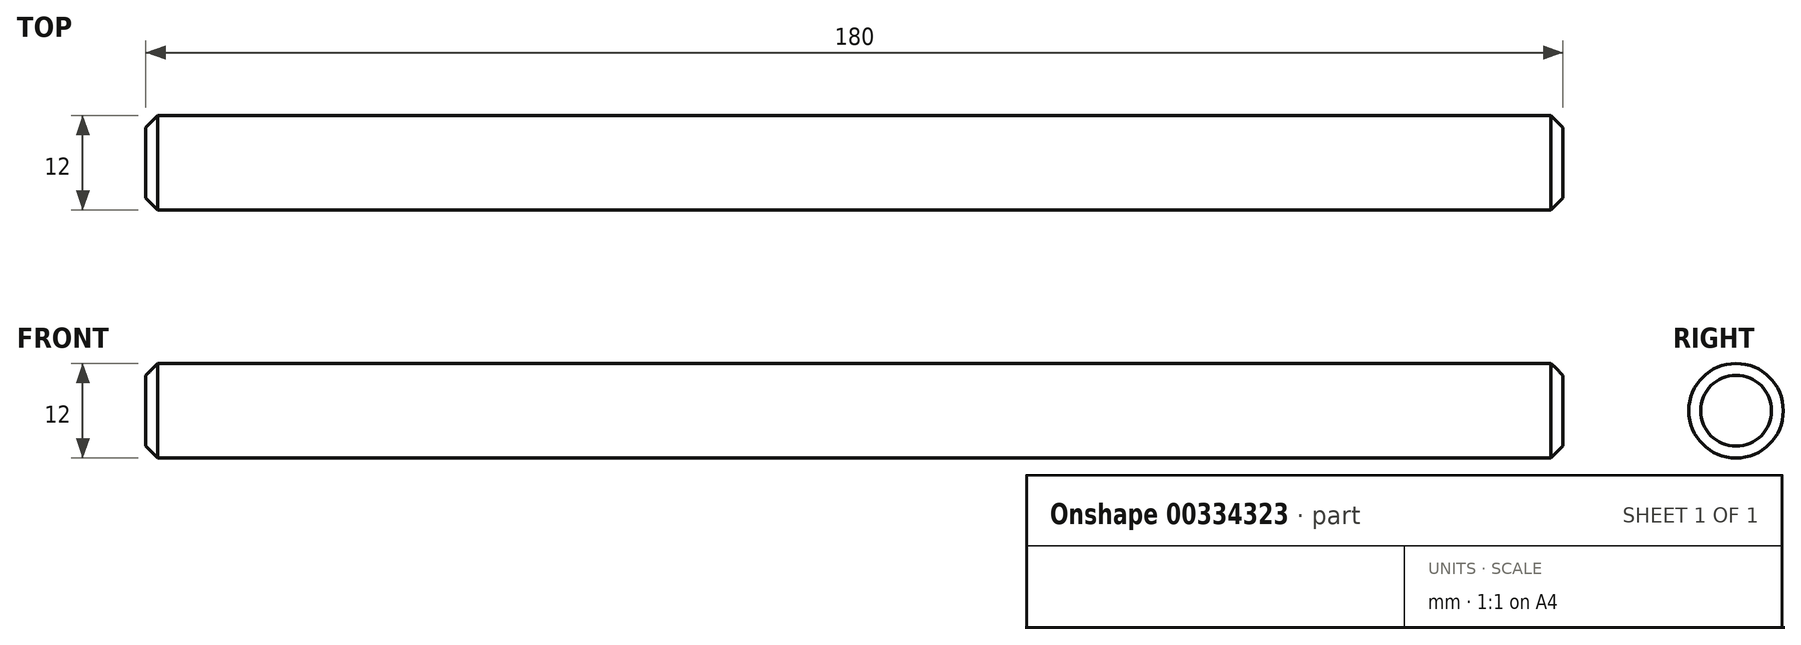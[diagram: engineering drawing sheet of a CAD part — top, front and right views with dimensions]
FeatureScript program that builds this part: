
annotation { "Feature Type Name" : "Feature", "Feature Type Description" : "" }
export const myFeature = defineFeature(function(context is Context, id is Id, definition is map)
    precondition{}
    {
        {
            var Q0;
            Q0=qCreatedBy(makeId("Front.planeOp"),FACE);
            var sketch = newSketch(context, id + "F0", { "sketchPlane" : qUnion([Q0])});
            skLineSegment(sketch, "E0", {"start": v(0, 0) * mm, "end": v(0, 4.5) * mm});
            skLineSegment(sketch, "E1", {"start": v(0, 4.5) * mm, "end": v(1.5, 6) * mm});
            skLineSegment(sketch, "E2", {"start": v(1.5, 6) * mm, "end": v(178.5, 6) * mm});
            skLineSegment(sketch, "E3", {"start": v(178.5, 6) * mm, "end": v(180, 4.5) * mm});
            skLineSegment(sketch, "E4", {"start": v(180, 4.5) * mm, "end": v(180, 0) * mm});
            skLineSegment(sketch, "E5", {"start": v(-4.1, 0) * mm, "end": v(217.64, 0) * mm, "construction": true});
            skLineSegment(sketch, "E6", {"start": v(0, 0) * mm, "end": v(180, 0) * mm});
            skSolve(sketch);
        }
        {
            var Q0;
            Q0=makeQuery(id+"F0.imprint","IMPRINT",FACE,{"disambiguationData":[TD([[makeQuery(id+"F0.imprint","IMPRINT",EDGE,{"derivedFrom":sQuery(id+"F0.wireOp",EDGE,"E0")}),-1.0]])]});
            var Q1;
            Q1=sQuery(id+"F0.wireOp",EDGE,"E5");
            revolve(context, id + "F1", {"entities" : qUnion([Q0]), "axis" : qUnion([Q1]), "revolveType" : RevolveType.FULL});
        }
    });
